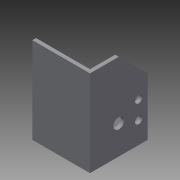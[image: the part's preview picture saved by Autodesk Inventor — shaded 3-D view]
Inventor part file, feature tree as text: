
AUTODESK INVENTOR PART (.ipt)
format: ipt  version: 2015 SP1 (Build 190203100, 203)  size: 122,880 bytes
history: native  units: in
note: dims shown in document units (in); Inventor stores cm internally (conversion verified against a paired STEP export)
features: sketch x4, extrude x2, hole x2
ambient origin geometry x8: Origin, YZ Plane, XZ Plane, XY Plane, X Axis, Y Axis, Z Axis, Center Point
bodies: Solid1 (feature_tree)
feature tree (8):
  extrude  "Extrusion1"  Depth=0.125in
  hole  "Hole1"  [1 undecoded]
  hole  "Hole2"  [1 undecoded]
  extrude  "Extrusion4"  Depth=3.0in
  sketch  "Sketch1"  dims[d0=2.0in d1=0.125in]
  sketch  "Sketch4"  dims[d2=0.125in d3=2.0in]
  sketch  "Sketch5"  dims[d4=3.0in d5=0.0in d11=1.0in]
  sketch  "Sketch6"  dims[d12=1.0in d13=0.375in d14=0.75in d15=0.375in d16=0.25in d17=0.5635in d18=1.0in d19=0.8108in d20=0.375in d21=0.25in d23=0.3125in d24=0.3125in d25=0.25in d26=0.75in d27=0.375in d28=0.25in d29=0.5635in d30=1.0in d31=0.8108in d32=1.0in d33=45.0deg d34=3.0in d35=0.0in]
note: 2 required parameter values undecoded (feature->parameter linkage not recoverable at this tier; creation-order binding heuristic only, values carry confidence <= 0.55)
